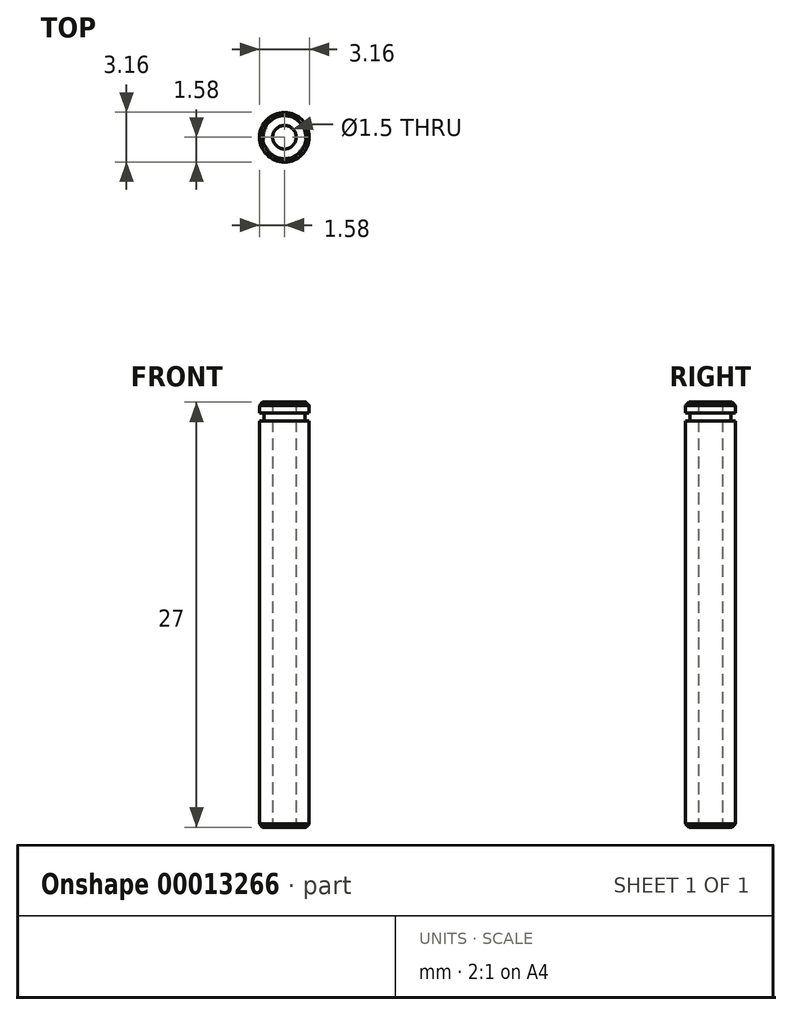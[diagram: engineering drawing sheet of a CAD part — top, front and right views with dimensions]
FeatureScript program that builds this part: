
annotation { "Feature Type Name" : "Feature", "Feature Type Description" : "" }
export const myFeature = defineFeature(function(context is Context, id is Id, definition is map)
    precondition{}
    {
        {
            var Q0;
            Q0=qCreatedBy(makeId("Top.planeOp"),FACE);
            var sketch = newSketch(context, id + "F0", { "sketchPlane" : qUnion([Q0])});
            skCircle(sketch, "E0", {"center": v(0, 0) * mm, "radius": 1.57 * mm});
            skCircle(sketch, "E1", {"center": v(0, 0) * mm, "radius": 0.75 * mm});
            skSolve(sketch);
        }
        {
            var Q0;
            Q0=makeQuery(id+"F0.imprint","IMPRINT",FACE,{"disambiguationData":[TD([[makeQuery(id+"F0.imprint","IMPRINT",EDGE,{"derivedFrom":sQuery(id+"F0.wireOp",EDGE,"E0")}),1.0]])]});
            extrude(context, id + "F1", {"entities" : qUnion([Q0]), "depth" : 27 * mm});
        }
        {
            var Q0;
            Q0=makeQuery(id+"F1.opExtrude","CAP_EDGE",EDGE,{"disambiguationData":[OSD([sQuery(id+"F0.wireOp",EDGE,"E0")])],"isStart":false});
            var Q1;
            Q1=makeQuery(id+"F1.opExtrude","CAP_EDGE",EDGE,{"disambiguationData":[OSD([sQuery(id+"F0.wireOp",EDGE,"E0")])],"isStart":true});
            chamfer(context, id + "F2", {"entities" : qUnion([Q0, Q1]), "width" : 0.2 * mm, "tangentPropagation" : true});
        }
        {
            var Q0;
            Q0=qCreatedBy(makeId("Front.planeOp"),FACE);
            var sketch = newSketch(context, id + "F3", { "sketchPlane" : qUnion([Q0])});
            skLineSegment(sketch, "E2.bottom", {"start": v(-1.3, 26.3) * mm, "end": v(-1.7, 26.3) * mm});
            skLineSegment(sketch, "E2.top", {"start": v(-1.3, 25.8) * mm, "end": v(-1.7, 25.8) * mm});
            skLineSegment(sketch, "E2.left", {"start": v(-1.3, 26.3) * mm, "end": v(-1.3, 25.8) * mm});
            skLineSegment(sketch, "E2.right", {"start": v(-1.7, 26.3) * mm, "end": v(-1.7, 25.8) * mm});
            skLineSegment(sketch, "E3", {"start": v(0, 25.8) * mm, "end": v(-1.3, 25.8) * mm, "construction": true});
            skLineSegment(sketch, "E4", {"start": v(0, 25.8) * mm, "end": v(0, 27.38) * mm, "construction": true});
            skSolve(sketch);
        }
        {
            var Q0;
            Q0=makeQuery(id+"F3.imprint","IMPRINT",FACE,{"disambiguationData":[TD([[makeQuery(id+"F3.imprint","IMPRINT",EDGE,{"derivedFrom":sQuery(id+"F3.wireOp",EDGE,"E2.bottom")}),1.0]])]});
            var Q1;
            Q1=sQuery(id+"F3.wireOp",EDGE,"E4");
            revolve(context, id + "F4", {"operationType" : NewBodyOperationType.REMOVE, "entities" : qUnion([Q0]), "axis" : qUnion([Q1]), "revolveType" : RevolveType.FULL, "oppositeDirection" : true});
        }
    });
